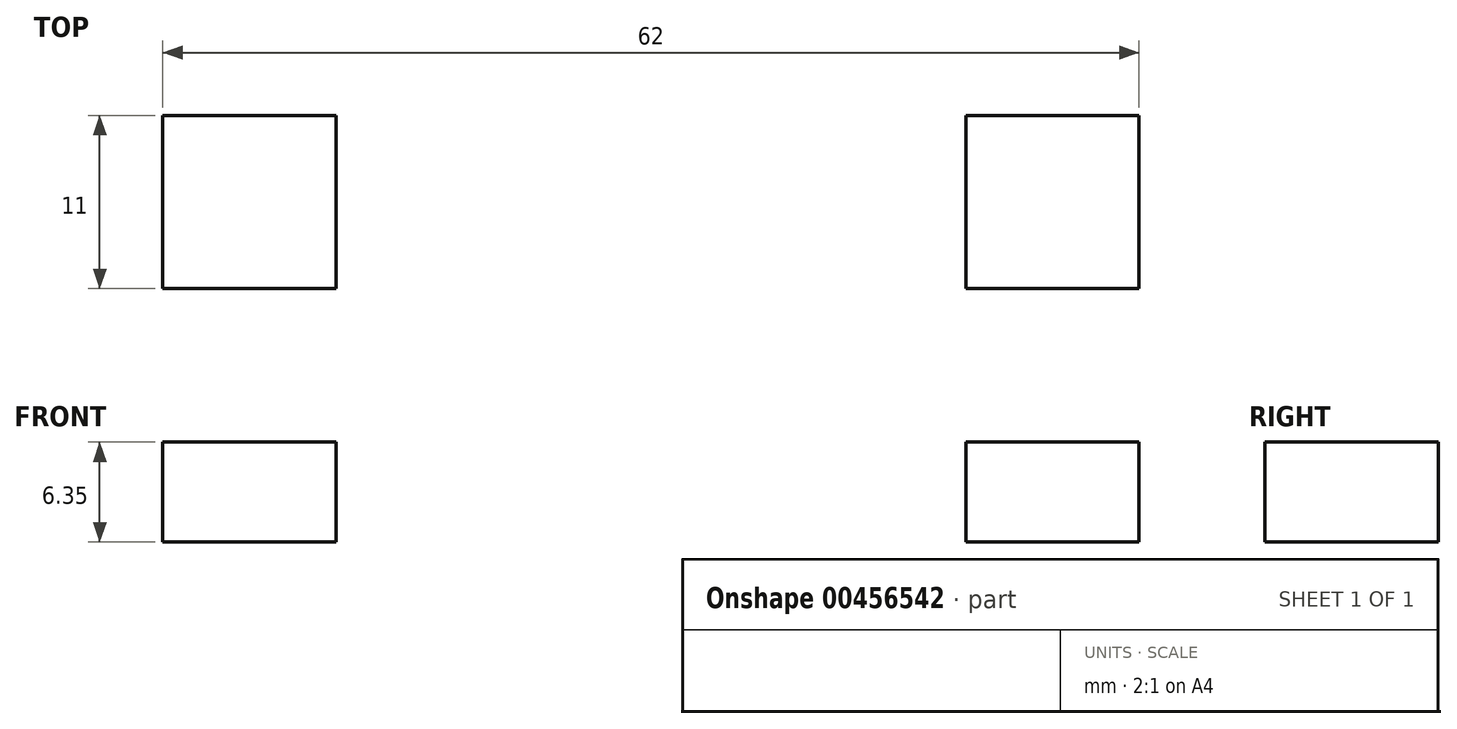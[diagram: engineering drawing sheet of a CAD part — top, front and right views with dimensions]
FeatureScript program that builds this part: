
annotation { "Feature Type Name" : "Feature", "Feature Type Description" : "" }
export const myFeature = defineFeature(function(context is Context, id is Id, definition is map)
    precondition{}
    {
        {
            var Q0;
            Q0=qCreatedBy(makeId("Top.planeOp"),FACE);
            var sketch = newSketch(context, id + "F0", { "sketchPlane" : qUnion([Q0])});
            skLineSegment(sketch, "E0.bottom", {"start": v(31, 56) * mm, "end": v(-31, 56) * mm});
            skLineSegment(sketch, "E0.top", {"start": v(31, -56) * mm, "end": v(-31, -56) * mm});
            skLineSegment(sketch, "E0.left", {"start": v(31, 56) * mm, "end": v(31, -56) * mm});
            skLineSegment(sketch, "E0.right", {"start": v(-31, 56) * mm, "end": v(-31, -56) * mm});
            skPoint(sketch, "E0.middle", {"position": v(0, 0) * mm});
            skCircle(sketch, "E1", {"center": v(0, 0) * mm, "radius": 3.12 * mm});
            skLineSegment(sketch, "E2.bottom", {"start": v(25, 50) * mm, "end": v(-25, 50) * mm, "construction": true});
            skLineSegment(sketch, "E2.top", {"start": v(25, -50) * mm, "end": v(-25, -50) * mm, "construction": true});
            skLineSegment(sketch, "E2.left", {"start": v(25, 50) * mm, "end": v(25, -50) * mm, "construction": true});
            skLineSegment(sketch, "E2.right", {"start": v(-25, 50) * mm, "end": v(-25, -50) * mm, "construction": true});
            skLineSegment(sketch, "E3.bottom", {"start": v(-31, 56) * mm, "end": v(-20, 56) * mm});
            skLineSegment(sketch, "E3.top", {"start": v(-31, 45) * mm, "end": v(-20, 45) * mm});
            skLineSegment(sketch, "E3.left", {"start": v(-31, 56) * mm, "end": v(-31, 45) * mm});
            skLineSegment(sketch, "E3.right", {"start": v(-20, 56) * mm, "end": v(-20, 45) * mm});
            skLineSegment(sketch, "E4.bottom", {"start": v(31, 56) * mm, "end": v(20, 56) * mm});
            skLineSegment(sketch, "E4.top", {"start": v(31, 45) * mm, "end": v(20, 45) * mm});
            skLineSegment(sketch, "E4.left", {"start": v(31, 56) * mm, "end": v(31, 45) * mm});
            skLineSegment(sketch, "E4.right", {"start": v(20, 56) * mm, "end": v(20, 45) * mm});
            skLineSegment(sketch, "E5.bottom", {"start": v(-31, -56) * mm, "end": v(-20, -56) * mm});
            skLineSegment(sketch, "E5.top", {"start": v(-31, -45) * mm, "end": v(-20, -45) * mm});
            skLineSegment(sketch, "E5.left", {"start": v(-31, -56) * mm, "end": v(-31, -45) * mm});
            skLineSegment(sketch, "E5.right", {"start": v(-20, -56) * mm, "end": v(-20, -45) * mm});
            skLineSegment(sketch, "E6.bottom", {"start": v(31, -56) * mm, "end": v(20, -56) * mm});
            skLineSegment(sketch, "E6.top", {"start": v(31, -45) * mm, "end": v(20, -45) * mm});
            skLineSegment(sketch, "E6.left", {"start": v(31, -56) * mm, "end": v(31, -45) * mm});
            skLineSegment(sketch, "E6.right", {"start": v(20, -56) * mm, "end": v(20, -45) * mm});
            skSolve(sketch);
        }
        {
            var Q0;
            Q0=makeQuery(id+"F0.imprint","IMPRINT",FACE,{"disambiguationData":[TD([[makeQuery(id+"F0.imprint","IMPRINT",EDGE,{"derivedFrom":sQuery(id+"F0.wireOp",EDGE,"E0.bottom")}),1.0]])]});
            extrude(context, id + "F1", {"entities" : qUnion([Q0]), "depth" : 6.35 * mm});
        }
    });
